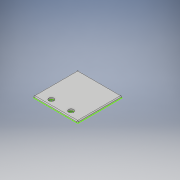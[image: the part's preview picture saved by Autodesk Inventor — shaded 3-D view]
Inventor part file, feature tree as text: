
AUTODESK INVENTOR PART (.ipt)
format: ipt  version: 2019 (Build 230136000, 136)  size: 155,136 bytes
history: native  units: in
note: dims shown in document units (in); Inventor stores cm internally (conversion verified against a paired STEP export)
features: extrude x6, fillet x2, other x1, sketch x1
ambient origin geometry x8: Origin, YZ Plane, XZ Plane, XY Plane, X Axis, Y Axis, Z Axis, Center Point
bodies: Solid1 (feature_tree)
feature tree (10):
  other  "ohisje_pokrov"
  sketch  "Sketch2"  dims[d8=2.126in d9=0.0787in d10=0.0787in d11=0.0787in d12=0.0787in d13=1.8898in d14=0.0394in d15=0.0394in d16=0.0394in d17=0.0394in d18=0.0787in d19=0.0in d20=0.0787in d21=0.0in d22=0.0394in d23=0.0394in d24=1.9685in d25=0.2402in d26=0.4724in d28=0.315in d29=0.9843in d30=0.9843in d31=0.0787in d32=0.0in d33=0.0787in d34=0.0in d35=0.0394in d36=0.0in d37=0.0394in d38=0.0in d39=0.1969in]
  extrude  "Extrusion1"  Depth=0.0787in
  extrude  "Extrusion2"  Depth=0.0787in
  fillet  "Fillet1"  Radius=0.0787in
  fillet  "Fillet2"  Radius=0.0787in
  extrude  "Extrusion3"  Depth=1.8898in
  extrude  "Extrusion4"  Depth=0.0394in
  extrude  "Extrusion5"  Depth=0.0394in
  extrude  "Extrusion6"  Depth=0.0394in
